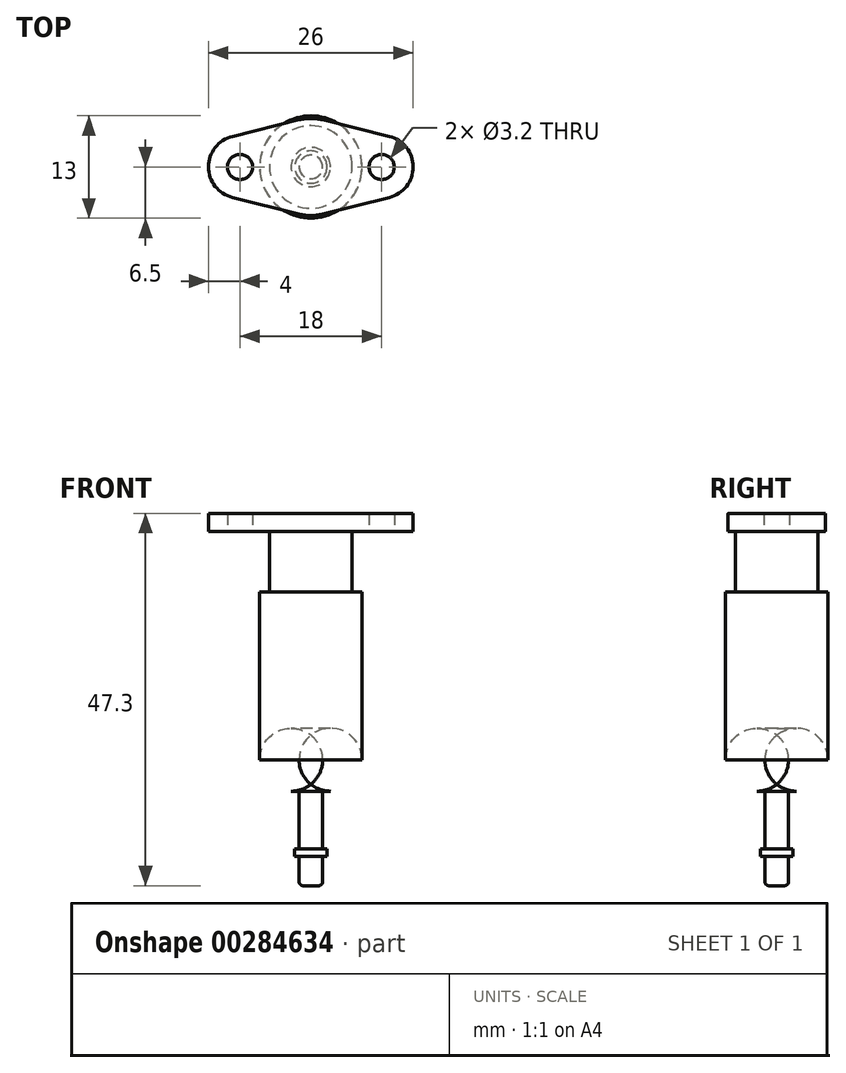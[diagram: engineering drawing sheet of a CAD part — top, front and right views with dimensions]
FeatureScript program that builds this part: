
annotation { "Feature Type Name" : "Feature", "Feature Type Description" : "" }
export const myFeature = defineFeature(function(context is Context, id is Id, definition is map)
    precondition{}
    {
        {
            var Q0;
            Q0=qCreatedBy(makeId("Front.planeOp"),FACE);
            var sketch = newSketch(context, id + "F0", { "sketchPlane" : qUnion([Q0])});
            skLineSegment(sketch, "E0.bottom", {"start": v(0, -3.7) * mm, "end": v(-1.5, -3.7) * mm});
            skLineSegment(sketch, "E0.top", {"start": v(0, 8.3) * mm, "end": v(-1.5, 8.3) * mm});
            skLineSegment(sketch, "E0.left", {"start": v(0, -3.7) * mm, "end": v(0, 8.3) * mm});
            skLineSegment(sketch, "E0.right", {"start": v(-1.5, -3.7) * mm, "end": v(-1.5, 8.3) * mm});
            skLineSegment(sketch, "E1", {"start": v(0, -3.7) * mm, "end": v(0, -16.82) * mm, "construction": true});
            skSolve(sketch);
        }
        {
            var Q0;
            Q0 = qSketchRegion(id + "F0", true);
            var Q1;
            Q1=sQuery(id+"F0.wireOp",EDGE,"E1");
            revolve(context, id + "F1", {"entities" : qUnion([Q0]), "axis" : qUnion([Q1]), "revolveType" : RevolveType.FULL});
        }
        {
            var Q0;
            Q0=makeQuery(id+"F1.opRevolve","SWEPT_FACE",FACE,{"disambiguationData":[OSD([sQuery(id+"F0.wireOp",EDGE,"E0.top")])]});
            var sketch = newSketch(context, id + "F2", { "sketchPlane" : qUnion([Q0])});
            skCircle(sketch, "E2", {"center": v(0, 0) * mm, "radius": 6.5 * mm});
            skSolve(sketch);
        }
        {
            var Q0;
            Q0 = qSketchRegion(id + "F2", true);
            extrude(context, id + "F3", {"entities" : qUnion([Q0]), "operationType" : NewBodyOperationType.ADD, "depth" : 25.3 * mm});
        }
        {
            var Q0;
            Q0=makeQuery(id+"F3.opExtrude","CAP_FACE",FACE,{"disambiguationData":[OSD([sQuery(id+"F2.wireOp",EDGE,"E2")])],"isStart":false});
            var sketch = newSketch(context, id + "F4", { "sketchPlane" : qUnion([Q0])});
            skCircle(sketch, "E3", {"center": v(0, 0) * mm, "radius": 5.25 * mm});
            skSolve(sketch);
        }
        {
            var Q0;
            Q0 = qSketchRegion(id + "F4", true);
            extrude(context, id + "F5", {"entities" : qUnion([Q0]), "operationType" : NewBodyOperationType.ADD, "depth" : 7.7 * mm});
        }
        {
            var Q0;
            Q0=makeQuery(id+"F5.opExtrude","CAP_FACE",FACE,{"disambiguationData":[OSD([sQuery(id+"F4.wireOp",EDGE,"E3")])],"isStart":false});
            var sketch = newSketch(context, id + "F6", { "sketchPlane" : qUnion([Q0])});
            skCircle(sketch, "E4", {"center": v(-9, 0) * mm, "radius": 1.6 * mm});
            skCircle(sketch, "E5", {"center": v(9, 0) * mm, "radius": 1.6 * mm});
            skArc(sketch, "E6", {"start": v(-9.97, 3.88) * mm, "mid": v(-13, 0) * mm, "end": v(-9.97, -3.88) * mm});
            skArc(sketch, "E7", {"start": v(9.97, -3.88) * mm, "mid": v(13, 0) * mm, "end": v(9.97, 3.88) * mm});
            skArc(sketch, "E8", {"start": v(-1.5, -6) * mm, "mid": v(0, -6.18) * mm, "end": v(1.5, -6) * mm});
            skLineSegment(sketch, "E9", {"start": v(-9.97, 3.88) * mm, "end": v(-1.5, 6) * mm});
            skLineSegment(sketch, "E10", {"start": v(-9.97, -3.88) * mm, "end": v(-1.5, -6) * mm});
            skLineSegment(sketch, "E11", {"start": v(1.5, 6) * mm, "end": v(9.97, 3.88) * mm});
            skLineSegment(sketch, "E12", {"start": v(1.5, -6) * mm, "end": v(9.97, -3.88) * mm});
            skArc(sketch, "E13.trimOffspring", {"start": v(1.5, 6) * mm, "mid": v(0, 6.18) * mm, "end": v(-1.5, 6) * mm});
            skSolve(sketch);
        }
        {
            var Q0;
            Q0 = qSketchRegion(id + "F6", true);
            extrude(context, id + "F7", {"entities" : qUnion([Q0]), "operationType" : NewBodyOperationType.ADD, "depth" : (10 - 7.7) * mm});
        }
        {
            var Q0;
            Q0=makeQuery(id+"F3.opExtrude","CAP_EDGE",EDGE,{"disambiguationData":[OSD([sQuery(id+"F2.wireOp",EDGE,"E2")])],"isStart":true});
            fillet(context, id + "F8", {"entities" : qUnion([Q0]), "radius" : 4 * mm, "tangentPropagation" : true, "allowEdgeOverflow" : false});
        }
        {
            var Q0;
            Q0=makeQuery(id+"F1.opRevolve","SWEPT_EDGE",EDGE,{"disambiguationData":[OSD([sQuery(id+"F0.wireOp",EDGE,"E0.bottom"),sQuery(id+"F0.wireOp",EDGE,"E0.right")])]});
            fillet(context, id + "F9", {"entities" : qUnion([Q0]), "radius" : .5 * mm, "tangentPropagation" : true, "allowEdgeOverflow" : false});
        }
        {
            var Q0;
            Q0=qCreatedBy(makeId("Top.planeOp"),FACE);
            var sketch = newSketch(context, id + "F10", { "sketchPlane" : qUnion([Q0])});
            skCircle(sketch, "E14", {"center": v(0, 0) * mm, "radius": 2.06 * mm});
            skSolve(sketch);
        }
        {
            var Q0;
            Q0 = qSketchRegion(id + "F10", true);
            extrude(context, id + "F11", {"entities" : qUnion([Q0]), "operationType" : NewBodyOperationType.ADD, "depth" : 1 * mm});
        }
    });
